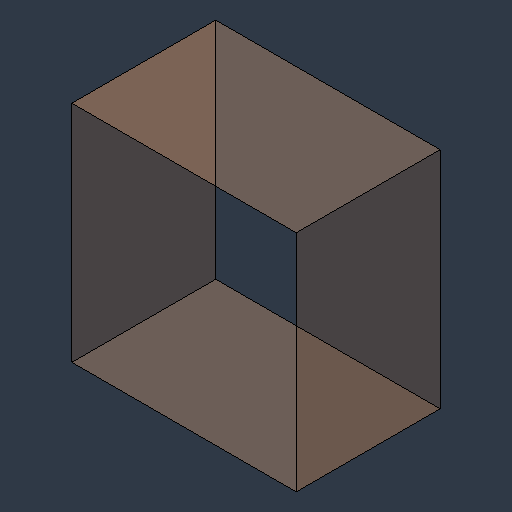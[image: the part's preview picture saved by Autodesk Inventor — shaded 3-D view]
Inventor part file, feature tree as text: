
AUTODESK INVENTOR PART (.ipt)
format: ipt  version: 2024.3 (Build 283343000, 343)  size: 87,552 bytes
history: native  units: mm (DEFAULTED — no unit token found)
features: sketch x1, other x1, extrude x1
ambient origin geometry x8: Origin, YZ Plane, XZ Plane, XY Plane, X Axis, Y Axis, Z Axis, Center Point
bodies: Body1 (feature_tree)
feature tree (3):
  sketch  "Sketch2"  dims[d0=749.3mm d1=457.2mm d2=1066.8mm d3=0.0mm]
  other  "Srf1"
  extrude  "ExtrusionSrf1"  Depth=457.2mm
